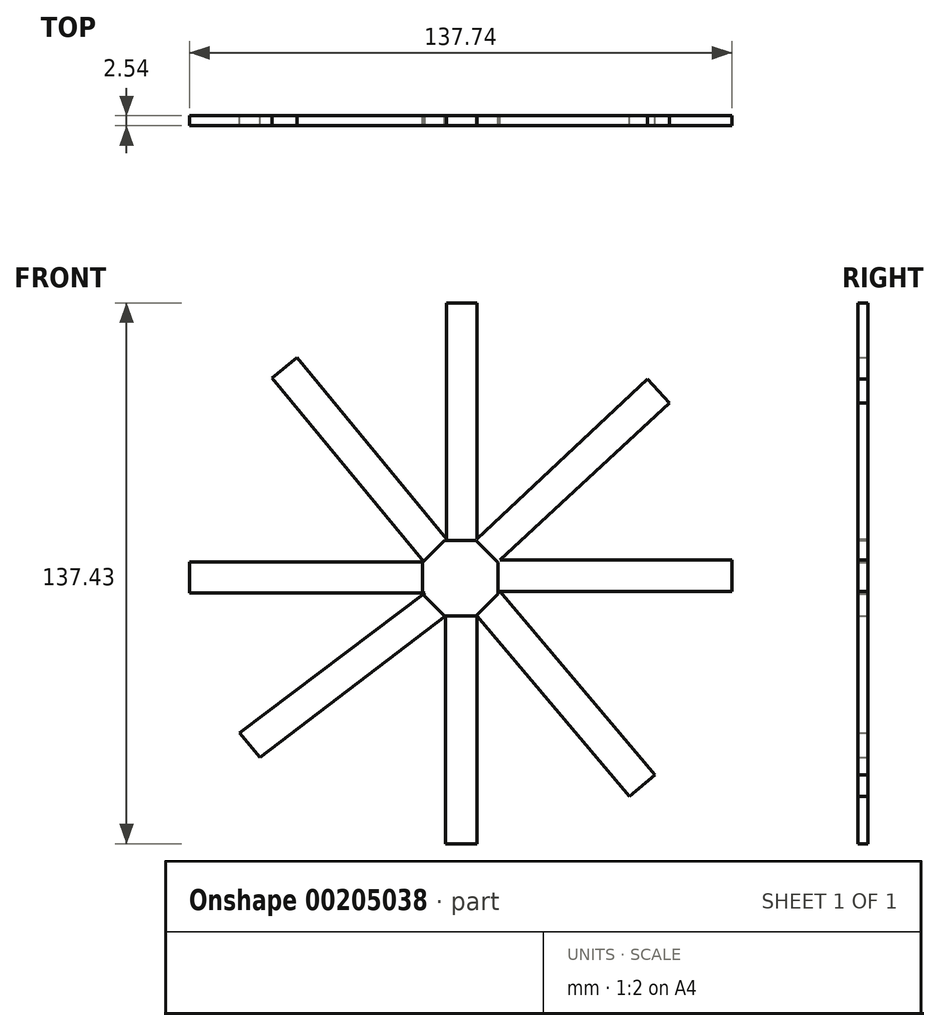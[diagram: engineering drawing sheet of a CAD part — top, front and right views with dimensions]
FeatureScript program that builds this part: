
annotation { "Feature Type Name" : "Feature", "Feature Type Description" : "" }
export const myFeature = defineFeature(function(context is Context, id is Id, definition is map)
    precondition{}
    {
        {
            var Q0;
            Q0=qCreatedBy(makeId("Front.planeOp"),FACE);
            var sketch = newSketch(context, id + "F0", { "sketchPlane" : qUnion([Q0])});
            skCircle(sketch, "E0.cCircle", {"center": v(0, 6.99) * mm, "radius": 10.4 * mm, "construction": true});
            skLineSegment(sketch, "E0.0", {"start": v(9.6, 10.97) * mm, "end": v(9.6, 3) * mm});
            skLineSegment(sketch, "E0.1", {"start": v(9.6, 3) * mm, "end": v(3.98, -2.62) * mm});
            skLineSegment(sketch, "E0.2", {"start": v(3.98, -2.62) * mm, "end": v(-3.98, -2.62) * mm});
            skLineSegment(sketch, "E0.3", {"start": v(-3.98, -2.62) * mm, "end": v(-9.6, 3) * mm});
            skLineSegment(sketch, "E0.4", {"start": v(-9.6, 3) * mm, "end": v(-9.6, 10.97) * mm});
            skLineSegment(sketch, "E0.5", {"start": v(-9.6, 10.97) * mm, "end": v(-3.98, 16.6) * mm});
            skLineSegment(sketch, "E0.6", {"start": v(-3.98, 16.6) * mm, "end": v(3.98, 16.6) * mm});
            skLineSegment(sketch, "E0.7", {"start": v(3.98, 16.6) * mm, "end": v(9.6, 10.97) * mm});
            skSolve(sketch);
        }
        {
            var Q0;
            Q0=makeQuery(id+"F0.imprint","IMPRINT",FACE,{"disambiguationData":[TD([[makeQuery(id+"F0.imprint","IMPRINT",EDGE,{"derivedFrom":sQuery(id+"F0.wireOp",EDGE,"E0.0")}),-1.0]])]});
            var sketch = newSketch(context, id + "F1", { "sketchPlane" : qUnion([Q0])});
            skLineSegment(sketch, "E1", {"start": v(4.27, 16.87) * mm, "end": v(4.27, 76.92) * mm});
            skLineSegment(sketch, "E2", {"start": v(4.58, 76.92) * mm, "end": v(-3.47, 76.92) * mm});
            skLineSegment(sketch, "E3", {"start": v(-3.47, 76.92) * mm, "end": v(-3.47, 16.87) * mm});
            skLineSegment(sketch, "E4", {"start": v(-3.47, 16.87) * mm, "end": v(-41.54, 62.99) * mm});
            skLineSegment(sketch, "E5", {"start": v(-41.54, 62.99) * mm, "end": v(-47.8, 57.82) * mm});
            skLineSegment(sketch, "E6", {"start": v(-47.8, 57.82) * mm, "end": v(-9.23, 11.09) * mm});
            skLineSegment(sketch, "E7", {"start": v(-9.23, 11.09) * mm, "end": v(-68.78, 11.09) * mm});
            skLineSegment(sketch, "E8", {"start": v(-68.78, 11.09) * mm, "end": v(-68.78, 3.25) * mm});
            skLineSegment(sketch, "E9", {"start": v(-68.78, 3.25) * mm, "end": v(-9.04, 3.25) * mm});
            skLineSegment(sketch, "E10", {"start": v(-3.78, -2.63) * mm, "end": v(-3.78, -60.5) * mm});
            skLineSegment(sketch, "E11", {"start": v(-3.78, -60.5) * mm, "end": v(4.27, -60.5) * mm});
            skLineSegment(sketch, "E12", {"start": v(4.27, -60.5) * mm, "end": v(4.27, -2.63) * mm});
            skLineSegment(sketch, "E13", {"start": v(4.27, -2.63) * mm, "end": v(42.96, -48.44) * mm});
            skLineSegment(sketch, "E14", {"start": v(42.96, -48.44) * mm, "end": v(49.4, -43) * mm});
            skLineSegment(sketch, "E15", {"start": v(49.4, -43) * mm, "end": v(10.03, 3.62) * mm});
            skLineSegment(sketch, "E16", {"start": v(10.03, 3.62) * mm, "end": v(68.96, 3.62) * mm});
            skLineSegment(sketch, "E17", {"start": v(68.96, 11.6) * mm, "end": v(68.96, 3.62) * mm});
            skLineSegment(sketch, "E18", {"start": v(68.96, 11.6) * mm, "end": v(10.03, 11.6) * mm});
            skLineSegment(sketch, "E19", {"start": v(10.03, 11.6) * mm, "end": v(53.18, 51.54) * mm});
            skLineSegment(sketch, "E20", {"start": v(53.18, 51.54) * mm, "end": v(47.54, 57.62) * mm});
            skLineSegment(sketch, "E21", {"start": v(47.54, 57.62) * mm, "end": v(4.27, 16.87) * mm});
            skLineSegment(sketch, "E22", {"start": v(-9.04, 3.25) * mm, "end": v(-56.1, -32.34) * mm});
            skLineSegment(sketch, "E23", {"start": v(-56.1, -32.34) * mm, "end": v(-50.85, -38.55) * mm});
            skLineSegment(sketch, "E24", {"start": v(-50.85, -38.55) * mm, "end": v(-3.78, -2.63) * mm});
            skSolve(sketch);
        }
        {
            var Q0;
            Q0 = qSketchRegion(id + "F0", true);
            var Q1;
            Q1 = qSketchRegion(id + "F1", true);
            extrude(context, id + "F2", {"entities" : qUnion([Q0, Q1]), "depth" : 2.54 * mm});
        }
    });
